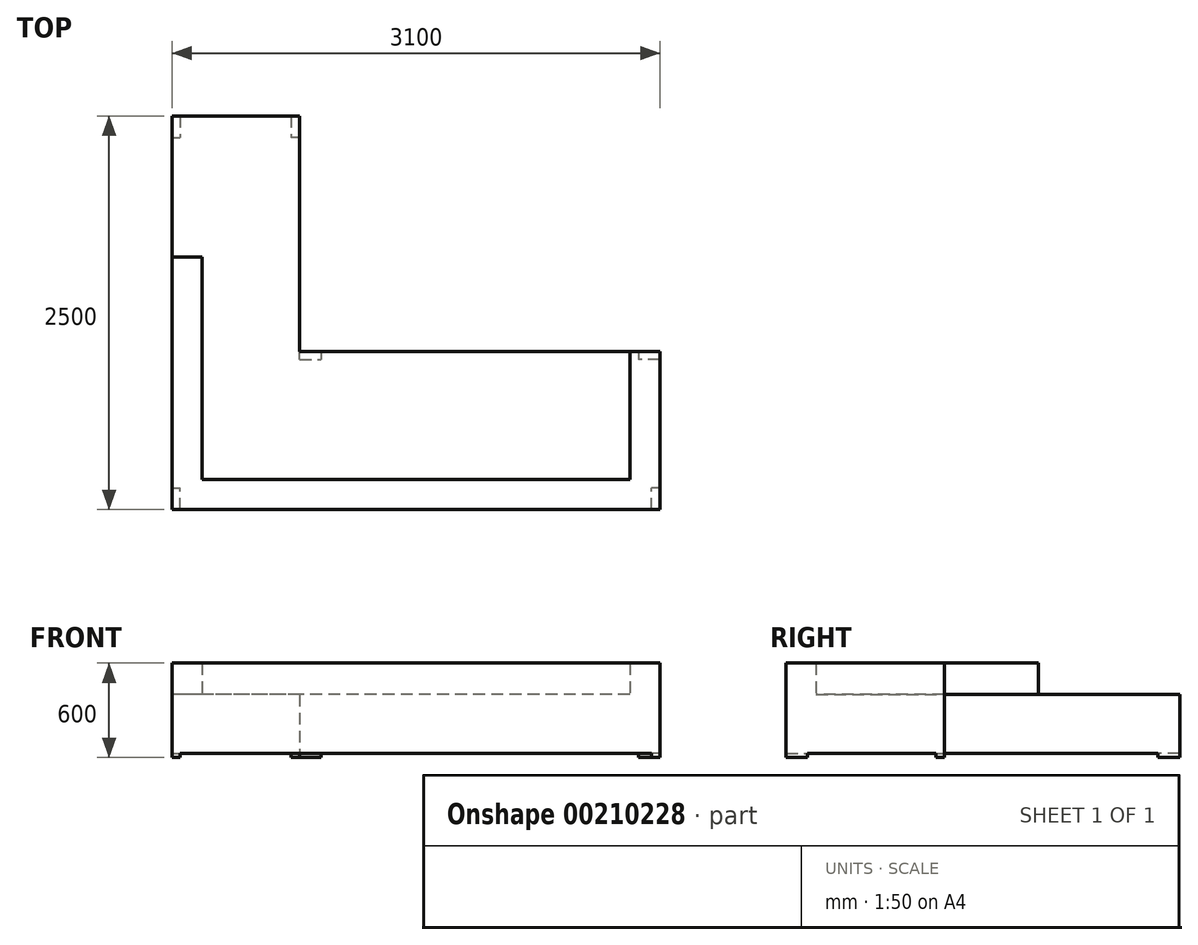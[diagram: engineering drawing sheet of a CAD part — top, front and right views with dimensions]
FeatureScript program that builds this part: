
annotation { "Feature Type Name" : "Feature", "Feature Type Description" : "" }
export const myFeature = defineFeature(function(context is Context, id is Id, definition is map)
    precondition{}
    {
        {
            var Q0;
            Q0=qCreatedBy(makeId("Top.planeOp"),FACE);
            var sketch = newSketch(context, id + "F0", { "sketchPlane" : qUnion([Q0])});
            skLineSegment(sketch, "E0", {"start": v(0, 0) * mm, "end": v(3100, 0) * mm});
            skLineSegment(sketch, "E1", {"start": v(3100, 0) * mm, "end": v(3100, 1004.66) * mm});
            skLineSegment(sketch, "E2", {"start": v(3100, 1004.66) * mm, "end": v(810.77, 1004.66) * mm});
            skLineSegment(sketch, "E3", {"start": v(810.77, 1004.66) * mm, "end": v(810.77, 2500) * mm});
            skLineSegment(sketch, "E4", {"start": v(810.77, 2500) * mm, "end": v(0, 2500) * mm});
            skLineSegment(sketch, "E5", {"start": v(0, 2500) * mm, "end": v(0, 0) * mm});
            skSolve(sketch);
        }
        {
            var Q0;
            Q0=makeQuery(id+"F0.imprint","IMPRINT",FACE,{"disambiguationData":[TD([[makeQuery(id+"F0.imprint","IMPRINT",EDGE,{"derivedFrom":sQuery(id+"F0.wireOp",EDGE,"E0")}),1.0]])]});
            extrude(context, id + "F1", {"entities" : qUnion([Q0]), "depth" : 400 * mm});
        }
        {
            var Q0;
            Q0=makeQuery(id+"F1.opExtrude","CAP_FACE",FACE,{"disambiguationData":[OSD([sQuery(id+"F0.wireOp",EDGE,"E0"),sQuery(id+"F0.wireOp",EDGE,"E1"),sQuery(id+"F0.wireOp",EDGE,"E2"),sQuery(id+"F0.wireOp",EDGE,"E3"),sQuery(id+"F0.wireOp",EDGE,"E4"),sQuery(id+"F0.wireOp",EDGE,"E5")])],"isStart":true});
            var sketch = newSketch(context, id + "F2", { "sketchPlane" : qUnion([Q0])});
            skLineSegment(sketch, "E6.bottom", {"start": v(0, 0) * mm, "end": v(52.93, 0) * mm});
            skLineSegment(sketch, "E6.top", {"start": v(0, -137.64) * mm, "end": v(52.93, -137.64) * mm});
            skLineSegment(sketch, "E6.left", {"start": v(0, 0) * mm, "end": v(0, -137.64) * mm});
            skLineSegment(sketch, "E6.right", {"start": v(52.93, 0) * mm, "end": v(52.93, -137.64) * mm});
            skLineSegment(sketch, "E7.bottom", {"start": v(0, -2500) * mm, "end": v(52.93, -2500) * mm});
            skLineSegment(sketch, "E7.top", {"start": v(0, -2362.36) * mm, "end": v(52.93, -2362.36) * mm});
            skLineSegment(sketch, "E7.left", {"start": v(0, -2500) * mm, "end": v(0, -2362.36) * mm});
            skLineSegment(sketch, "E7.right", {"start": v(52.93, -2500) * mm, "end": v(52.93, -2362.36) * mm});
            skLineSegment(sketch, "E8.bottom", {"start": v(810.77, -2500) * mm, "end": v(757.84, -2500) * mm});
            skLineSegment(sketch, "E8.top", {"start": v(810.77, -2362.36) * mm, "end": v(757.84, -2362.36) * mm});
            skLineSegment(sketch, "E8.left", {"start": v(810.77, -2500) * mm, "end": v(810.77, -2362.36) * mm});
            skLineSegment(sketch, "E8.right", {"start": v(757.84, -2500) * mm, "end": v(757.84, -2362.36) * mm});
            skLineSegment(sketch, "E9.bottom", {"start": v(810.77, -1004.66) * mm, "end": v(948.4, -1004.66) * mm});
            skLineSegment(sketch, "E9.top", {"start": v(810.77, -951.73) * mm, "end": v(948.4, -951.73) * mm});
            skLineSegment(sketch, "E9.left", {"start": v(810.77, -1004.66) * mm, "end": v(810.77, -951.73) * mm});
            skLineSegment(sketch, "E9.right", {"start": v(948.4, -1004.66) * mm, "end": v(948.4, -951.73) * mm});
            skLineSegment(sketch, "E10.bottom", {"start": v(3100, -1004.66) * mm, "end": v(2962.36, -1004.66) * mm});
            skLineSegment(sketch, "E10.top", {"start": v(3100, -951.73) * mm, "end": v(2962.36, -951.73) * mm});
            skLineSegment(sketch, "E10.left", {"start": v(3100, -1004.66) * mm, "end": v(3100, -951.73) * mm});
            skLineSegment(sketch, "E10.right", {"start": v(2962.36, -1004.66) * mm, "end": v(2962.36, -951.73) * mm});
            skLineSegment(sketch, "E11.bottom", {"start": v(3100, 0) * mm, "end": v(3047.07, 0) * mm});
            skLineSegment(sketch, "E11.top", {"start": v(3100, -137.64) * mm, "end": v(3047.07, -137.64) * mm});
            skLineSegment(sketch, "E11.left", {"start": v(3100, 0) * mm, "end": v(3100, -137.64) * mm});
            skLineSegment(sketch, "E11.right", {"start": v(3047.07, 0) * mm, "end": v(3047.07, -137.64) * mm});
            skSolve(sketch);
        }
        {
            var Q0;
            {var subQ4=sQuery(id+"F2.wireOp",EDGE,"E6.top");Q0=makeQuery(id+"F2.imprint","IMPRINT",FACE,{"disambiguationData":[TD([[makeQuery(id+"F2.imprint","IMPRINT",EDGE,{"derivedFrom":subQ4}),-1.0]])]});}
            extrude(context, id + "F3", {"entities" : qUnion([Q0]), "operationType" : NewBodyOperationType.REMOVE, "oppositeDirection" : true, "depth" : 25 * mm});
        }
        {
            var Q0;
            Q0=makeQuery(id+"F1.opExtrude","CAP_FACE",FACE,{"disambiguationData":[OSD([sQuery(id+"F0.wireOp",EDGE,"E0"),sQuery(id+"F0.wireOp",EDGE,"E1"),sQuery(id+"F0.wireOp",EDGE,"E2"),sQuery(id+"F0.wireOp",EDGE,"E3"),sQuery(id+"F0.wireOp",EDGE,"E4"),sQuery(id+"F0.wireOp",EDGE,"E5")])],"isStart":false});
            var sketch = newSketch(context, id + "F4", { "sketchPlane" : qUnion([Q0])});
            skLineSegment(sketch, "E12.0", {"start": v(0, 0) * mm, "end": v(3100, 0) * mm});
            skLineSegment(sketch, "E13.0", {"start": v(3100, 0) * mm, "end": v(3100, 1004.66) * mm});
            skLineSegment(sketch, "E14", {"start": v(3100, 1004.66) * mm, "end": v(2908.66, 1004.66) * mm});
            skLineSegment(sketch, "E15", {"start": v(2908.66, 1004.66) * mm, "end": v(2908.66, 191.34) * mm});
            skLineSegment(sketch, "E16", {"start": v(2908.66, 191.34) * mm, "end": v(191.34, 191.34) * mm});
            skLineSegment(sketch, "E17", {"start": v(191.34, 191.34) * mm, "end": v(191.34, 1602.66) * mm});
            skLineSegment(sketch, "E18", {"start": v(191.34, 1602.66) * mm, "end": v(0, 1602.66) * mm});
            skLineSegment(sketch, "E19", {"start": v(0, 1602.66) * mm, "end": v(0, 0) * mm});
            skLineSegment(sketch, "E20", {"start": v(949.53, 191.34) * mm, "end": v(949.53, 0) * mm, "construction": true});
            skSolve(sketch);
        }
        {
            var Q0;
            Q0=makeQuery(id+"F4.imprint","IMPRINT",FACE,{"disambiguationData":[TD([[makeQuery(id+"F4.imprint","IMPRINT",EDGE,{"derivedFrom":sQuery(id+"F4.wireOp",EDGE,"E12.0")}),1.0]])]});
            extrude(context, id + "F5", {"entities" : qUnion([Q0]), "operationType" : NewBodyOperationType.ADD, "depth" : 200 * mm});
        }
    });
